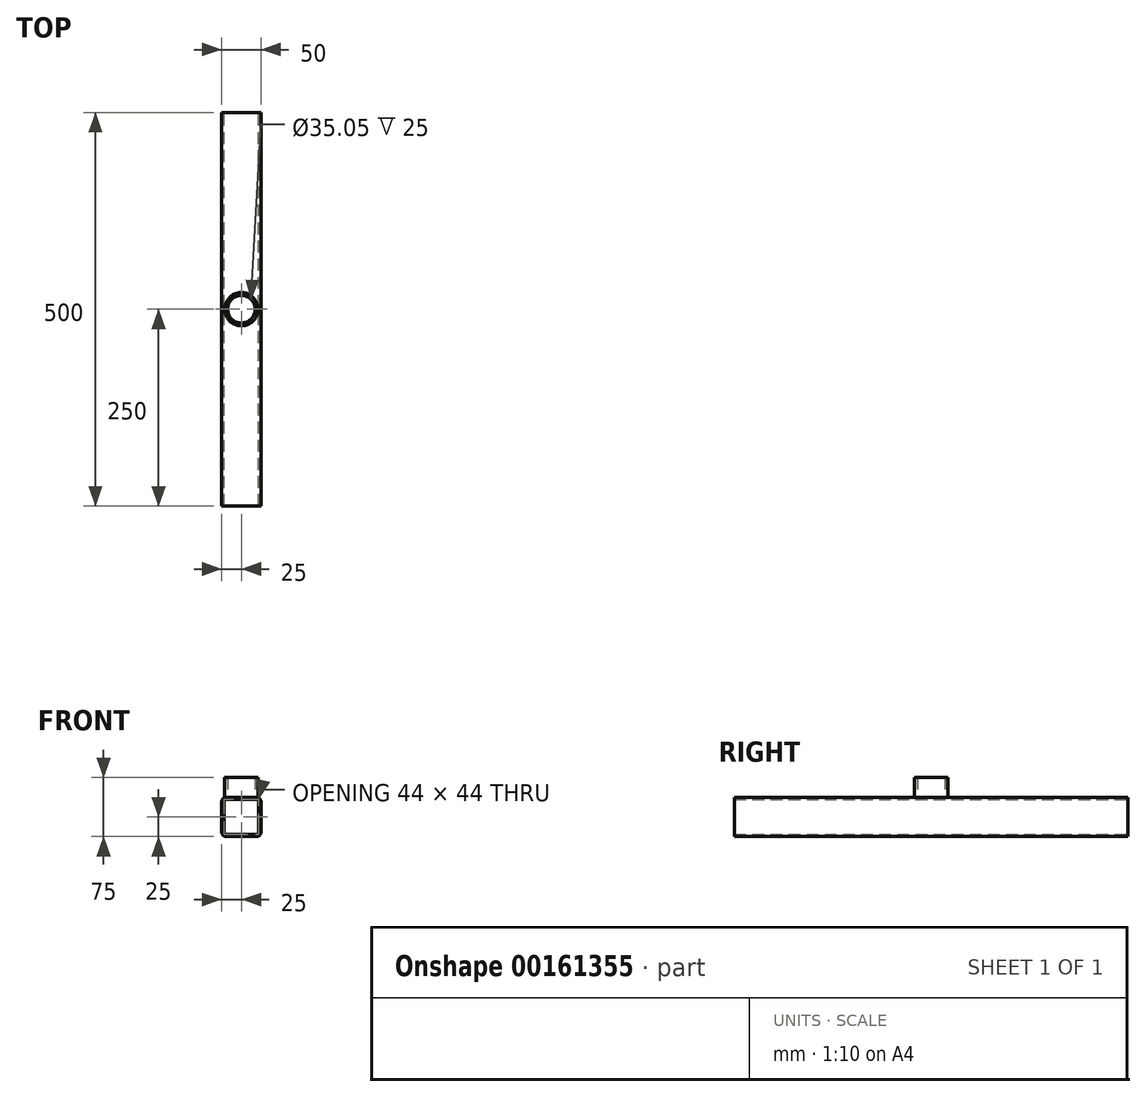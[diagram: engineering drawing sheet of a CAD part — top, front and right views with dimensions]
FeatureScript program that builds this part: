
annotation { "Feature Type Name" : "Feature", "Feature Type Description" : "" }
export const myFeature = defineFeature(function(context is Context, id is Id, definition is map)
    precondition{}
    {
        {
            var Q0;
            Q0=qCreatedBy(makeId("Front.planeOp"),FACE);
            var sketch = newSketch(context, id + "F0", { "sketchPlane" : qUnion([Q0])});
            skLineSegment(sketch, "E0.bottom", {"start": v(25, -25) * mm, "end": v(-25, -25) * mm});
            skLineSegment(sketch, "E0.top", {"start": v(25, 25) * mm, "end": v(-25, 25) * mm});
            skLineSegment(sketch, "E0.left", {"start": v(25, -25) * mm, "end": v(25, 25) * mm});
            skLineSegment(sketch, "E0.right", {"start": v(-25, -25) * mm, "end": v(-25, 25) * mm});
            skPoint(sketch, "E0.middle", {"position": v(0, 0) * mm});
            skSolve(sketch);
        }
        {
            var Q0;
            Q0=qSketchRegion(id+"F0",true);
            extrude(context, id + "F1", {"entities" : qUnion([Q0]), "depth" : 500 * mm});
        }
        {
            var Q0;
            Q0=makeQuery(id+"F1.opExtrude","SWEPT_EDGE",EDGE,{"disambiguationData":[OSD([sQuery(id+"F0.wireOp",EDGE,"E0.top"),sQuery(id+"F0.wireOp",EDGE,"E0.left")])]});
            var Q1;
            Q1=makeQuery(id+"F1.opExtrude","SWEPT_EDGE",EDGE,{"disambiguationData":[OSD([sQuery(id+"F0.wireOp",EDGE,"E0.top"),sQuery(id+"F0.wireOp",EDGE,"E0.right")])]});
            var Q2;
            Q2=makeQuery(id+"F1.opExtrude","SWEPT_EDGE",EDGE,{"disambiguationData":[OSD([sQuery(id+"F0.wireOp",EDGE,"E0.bottom"),sQuery(id+"F0.wireOp",EDGE,"E0.left")])]});
            var Q3;
            Q3=makeQuery(id+"F1.opExtrude","SWEPT_EDGE",EDGE,{"disambiguationData":[OSD([sQuery(id+"F0.wireOp",EDGE,"E0.bottom"),sQuery(id+"F0.wireOp",EDGE,"E0.right")])]});
            fillet(context, id + "F2", {"entities" : qUnion([Q0, Q1, Q2, Q3]), "radius" : 6 * mm, "tangentPropagation" : true, "allowEdgeOverflow" : false});
        }
        {
            var Q0;
            Q0=makeQuery(id+"F1.opExtrude","CAP_FACE",FACE,{"disambiguationData":[OSD([sQuery(id+"F0.wireOp",EDGE,"E0.bottom"),sQuery(id+"F0.wireOp",EDGE,"E0.top"),sQuery(id+"F0.wireOp",EDGE,"E0.left"),sQuery(id+"F0.wireOp",EDGE,"E0.right")])],"isStart":true});
            var Q1;
            Q1=makeQuery(id+"F1.opExtrude","CAP_FACE",FACE,{"disambiguationData":[OSD([sQuery(id+"F0.wireOp",EDGE,"E0.bottom"),sQuery(id+"F0.wireOp",EDGE,"E0.top"),sQuery(id+"F0.wireOp",EDGE,"E0.left"),sQuery(id+"F0.wireOp",EDGE,"E0.right")])],"isStart":false});
            shell(context, id + "F3", {"entities" : qUnion([Q0, Q1]), "thickness" : 3 * mm});
        }
        {
            var Q0;
            Q0=makeQuery(id+"F1.opExtrude","SWEPT_FACE",FACE,{"disambiguationData":[OSD([sQuery(id+"F0.wireOp",EDGE,"E0.top")])]});
            var sketch = newSketch(context, id + "F4", { "sketchPlane" : qUnion([Q0])});
            skLineSegment(sketch, "E1", {"start": v(0, 0) * mm, "end": v(0, -500) * mm, "construction": true});
            skCircle(sketch, "E2", {"center": v(0, -250) * mm, "radius": 21.08 * mm});
            skCircle(sketch, "E3", {"center": v(0, -250) * mm, "radius": 17.53 * mm});
            skSolve(sketch);
        }
        {
            var Q0;
            Q0=makeQuery(id+"F4.imprint","IMPRINT",FACE,{"disambiguationData":[TD([[makeQuery(id+"F4.imprint","IMPRINT",EDGE,{"derivedFrom":sQuery(id+"F4.wireOp",EDGE,"E2")}),1.0]])]});
            var Q1;
            {var subQ0=sQuery(id+"F4.wireOp",EDGE,"E2");var subQ1=sQuery(id+"F0.wireOp",EDGE,"E0.top");var subQ2=makeQuery(id+"F2.opFillet","BLEND_EDGE",EDGE,{"blendedFrom":[makeQuery(id+"F1.opExtrude","SWEPT_EDGE",EDGE,{"disambiguationData":[OSD([subQ1,sQuery(id+"F0.wireOp",EDGE,"E0.right")])]}),makeQuery(id+"F1.opExtrude","SWEPT_FACE",FACE,{"disambiguationData":[OSD([subQ1])]})],"blendedInto":[makeQuery(id+"F1.opExtrude","SWEPT_FACE",FACE,{"disambiguationData":[OSD([subQ1])]})]});var subQ3=makeQuery(id+"F4.imprint","INTERSECT",VERTEX,{"disambiguationData":[OD(0.0)],"derivedFrom":[subQ2,subQ0]});Q1=makeQuery(id+"F4.imprint","IMPRINT",FACE,{"disambiguationData":[TD([[makeQuery(id+"F4.imprint","IMPRINT",EDGE,{"disambiguationData":[TD([[subQ3,-1.0]])],"derivedFrom":subQ0}),1.0]])]});}
            var Q2;
            {var subQ0=sQuery(id+"F4.wireOp",EDGE,"E2");var subQ1=sQuery(id+"F0.wireOp",EDGE,"E0.top");var subQ2=makeQuery(id+"F2.opFillet","BLEND_EDGE",EDGE,{"blendedFrom":[makeQuery(id+"F1.opExtrude","SWEPT_EDGE",EDGE,{"disambiguationData":[OSD([subQ1,sQuery(id+"F0.wireOp",EDGE,"E0.left")])]}),makeQuery(id+"F1.opExtrude","SWEPT_FACE",FACE,{"disambiguationData":[OSD([subQ1])]})],"blendedInto":[makeQuery(id+"F1.opExtrude","SWEPT_FACE",FACE,{"disambiguationData":[OSD([subQ1])]})]});var subQ3=makeQuery(id+"F4.imprint","INTERSECT",VERTEX,{"disambiguationData":[OD(0.0)],"derivedFrom":[subQ2,subQ0]});Q2=makeQuery(id+"F4.imprint","IMPRINT",FACE,{"disambiguationData":[TD([[makeQuery(id+"F4.imprint","IMPRINT",EDGE,{"disambiguationData":[TD([[subQ3,1.0]])],"derivedFrom":subQ0}),1.0]])]});}
            extrude(context, id + "F5", {"entities" : qUnion([Q0, Q1, Q2]), "operationType" : NewBodyOperationType.ADD, "depth" : 25 * mm});
        }
    });
